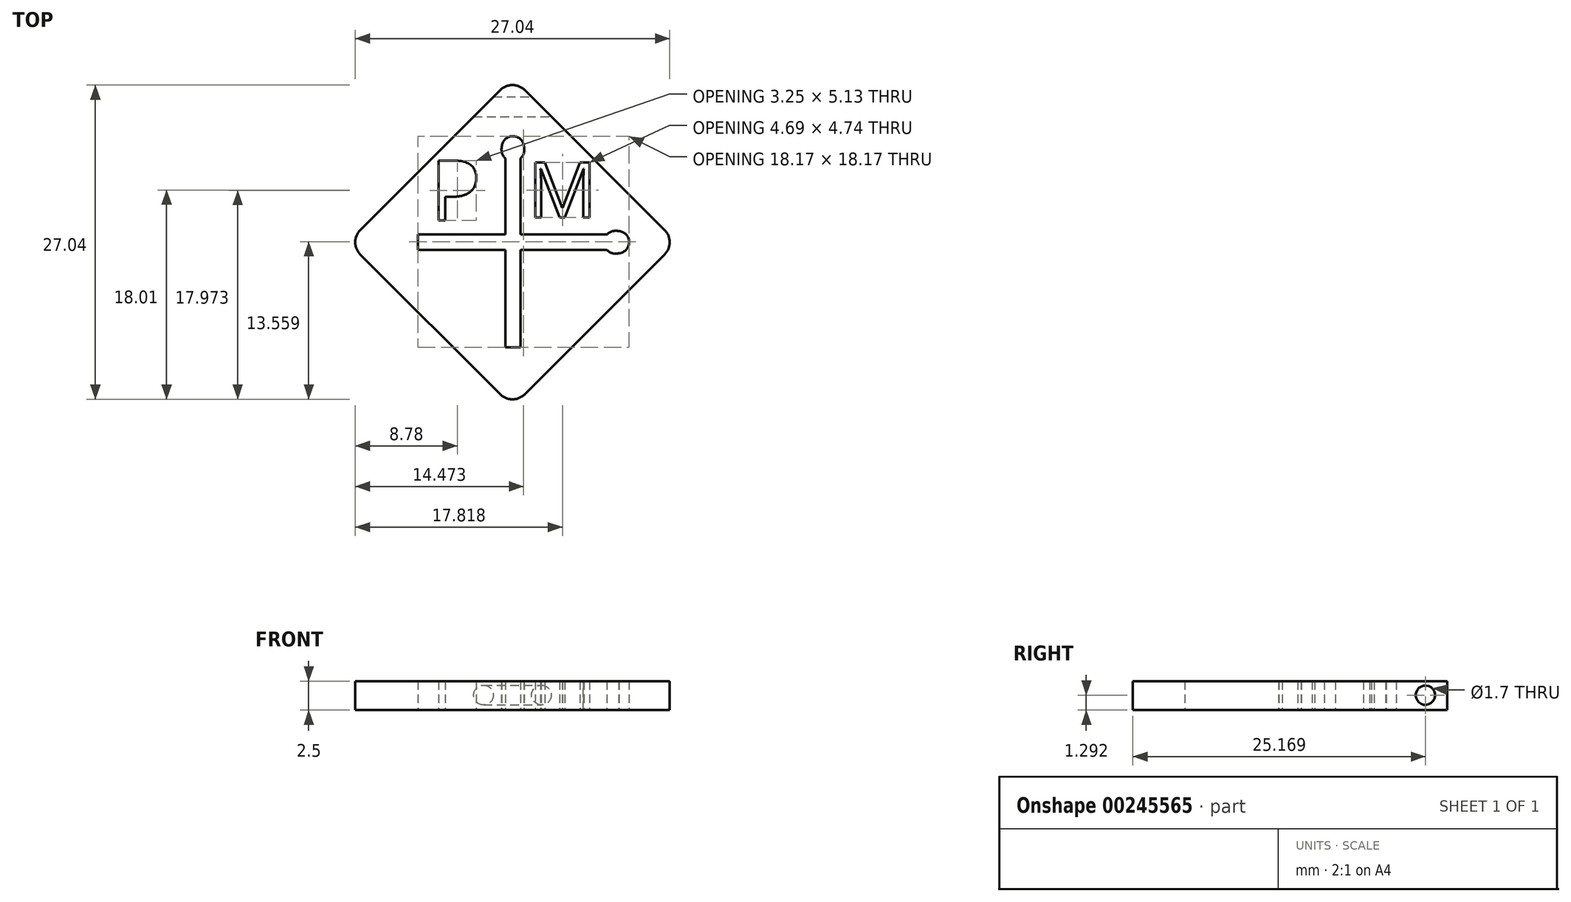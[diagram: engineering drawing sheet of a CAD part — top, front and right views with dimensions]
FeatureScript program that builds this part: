
annotation { "Feature Type Name" : "Feature", "Feature Type Description" : "" }
export const myFeature = defineFeature(function(context is Context, id is Id, definition is map)
    precondition{}
    {
        {
            var Q0;
            Q0=qCreatedBy(makeId("Top.planeOp"),FACE);
            var sketch = newSketch(context, id + "F0", { "sketchPlane" : qUnion([Q0])});
            skLineSegment(sketch, "E0", {"start": v(1.06, -1.06) * mm, "end": v(13.08, -13.08) * mm});
            skLineSegment(sketch, "E1", {"start": v(13.08, -15.2) * mm, "end": v(1.06, -27.22) * mm});
            skLineSegment(sketch, "E2", {"start": v(-1.06, -27.22) * mm, "end": v(-13.08, -15.2) * mm});
            skLineSegment(sketch, "E3", {"start": v(-13.08, -13.08) * mm, "end": v(-1.06, -1.06) * mm});
            skPoint(sketch, "E4.visualSharp", {"position": v(0, 0) * mm});
            skArc(sketch, "E4.filletArc", {"start": v(1.06, -1.06) * mm, "mid": v(0, -0.62) * mm, "end": v(-1.06, -1.06) * mm});
            skPoint(sketch, "E5.visualSharp", {"position": v(-14.14, -14.14) * mm});
            skArc(sketch, "E5.filletArc", {"start": v(-13.08, -13.08) * mm, "mid": v(-13.52, -14.14) * mm, "end": v(-13.08, -15.2) * mm});
            skPoint(sketch, "E6.visualSharp", {"position": v(14.14, -14.14) * mm});
            skArc(sketch, "E6.filletArc", {"start": v(13.08, -15.2) * mm, "mid": v(13.52, -14.14) * mm, "end": v(13.08, -13.08) * mm});
            skPoint(sketch, "E7.visualSharp", {"position": v(0, -28.28) * mm});
            skArc(sketch, "E7.filletArc", {"start": v(-1.06, -27.22) * mm, "mid": v(0, -27.66) * mm, "end": v(1.06, -27.22) * mm});
            skLineSegment(sketch, "E8", {"start": v(0, 0) * mm, "end": v(0, -31.86) * mm, "construction": true});
            skLineSegment(sketch, "E9", {"start": v(-14.14, -14.14) * mm, "end": v(14.14, -14.14) * mm, "construction": true});
            skLineSegment(sketch, "E10", {"start": v(-8.13, -13.48) * mm, "end": v(-8.13, -14.8) * mm});
            skLineSegment(sketch, "E11", {"start": v(-8.13, -14.8) * mm, "end": v(8.13, -14.8) * mm});
            skLineSegment(sketch, "E12", {"start": v(8.13, -13.48) * mm, "end": v(-8.13, -13.48) * mm});
            skLineSegment(sketch, "E13", {"start": v(-8.13, -13.48) * mm, "end": v(0, -13.48) * mm, "construction": true});
            skLineSegment(sketch, "E14", {"start": v(0, -13.48) * mm, "end": v(8.13, -13.48) * mm, "construction": true});
            skArc(sketch, "E15", {"start": v(9.18, -15.1) * mm, "mid": v(10.04, -14.12) * mm, "end": v(9.13, -13.2) * mm});
            skArc(sketch, "E16", {"start": v(9.13, -13.2) * mm, "mid": v(8.6, -13.2) * mm, "end": v(8.13, -13.48) * mm});
            skArc(sketch, "E17", {"start": v(8.13, -14.8) * mm, "mid": v(8.61, -15.1) * mm, "end": v(9.18, -15.1) * mm});
            skLineSegment(sketch, "E18", {"start": v(-0.62, -23.19) * mm, "end": v(0.7, -23.19) * mm});
            skLineSegment(sketch, "E19", {"start": v(0.7, -23.19) * mm, "end": v(0.7, -6.92) * mm});
            skLineSegment(sketch, "E20", {"start": v(-0.62, -6.92) * mm, "end": v(-0.62, -23.19) * mm});
            skLineSegment(sketch, "E21", {"start": v(-0.62, -23.19) * mm, "end": v(-0.62, -15.05) * mm, "construction": true});
            skLineSegment(sketch, "E22", {"start": v(-0.62, -15.05) * mm, "end": v(-0.62, -6.92) * mm, "construction": true});
            skArc(sketch, "E23", {"start": v(0.99, -5.88) * mm, "mid": v(0.02, -5.01) * mm, "end": v(-0.91, -5.92) * mm});
            skArc(sketch, "E24", {"start": v(-0.91, -5.92) * mm, "mid": v(-0.9, -6.46) * mm, "end": v(-0.62, -6.92) * mm});
            skArc(sketch, "E25", {"start": v(0.7, -6.92) * mm, "mid": v(1, -6.44) * mm, "end": v(0.99, -5.88) * mm});
            skText(sketch, "E26", { "text": "P\n", "fontName": "OpenSans-Regular.ttf"});
            skText(sketch, "E27", { "text": "M", "fontName": "OpenSans-Regular.ttf"});
            skPoint(sketch, "E28", {"position": v(7.07, -7.07) * mm});
            const initialGuessF0  = {"E26": [-0.00707, -0.01225, 1, 0, 0.00517], "E27": [0.0013, -0.01202, 1, 0, 0.00478]};
            skSetInitialGuess(sketch, initialGuessF0);
            skSolve(sketch);
        }
        {
            var Q0;
            Q0=makeQuery(id+"F0.imprint","IMPRINT",FACE,{"disambiguationData":[TD([[makeQuery(id+"F0.imprint","IMPRINT",EDGE,{"derivedFrom":sQuery(id+"F0.wireOp",EDGE,"E0")}),-1.0]])]});
            extrude(context, id + "F1", {"entities" : qUnion([Q0]), "depth" : 2.5 * mm});
        }
        {
            var Q0;
            Q0=qCreatedBy(makeId("Right.planeOp"),FACE);
            var sketch = newSketch(context, id + "F2", { "sketchPlane" : qUnion([Q0])});
            skCircle(sketch, "E29", {"center": v(-2.5, 1.3) * mm, "radius": 0.85 * mm});
            skSolve(sketch);
        }
        {
            var Q0;
            Q0=qSketchRegion(id+"F2",true);
            extrude(context, id + "F3", {"entities" : qUnion([Q0]), "operationType" : NewBodyOperationType.REMOVE, "endBound" : BoundingType.SYMMETRIC, "oppositeDirection" : true, "depth" : 25 * mm});
        }
    });
